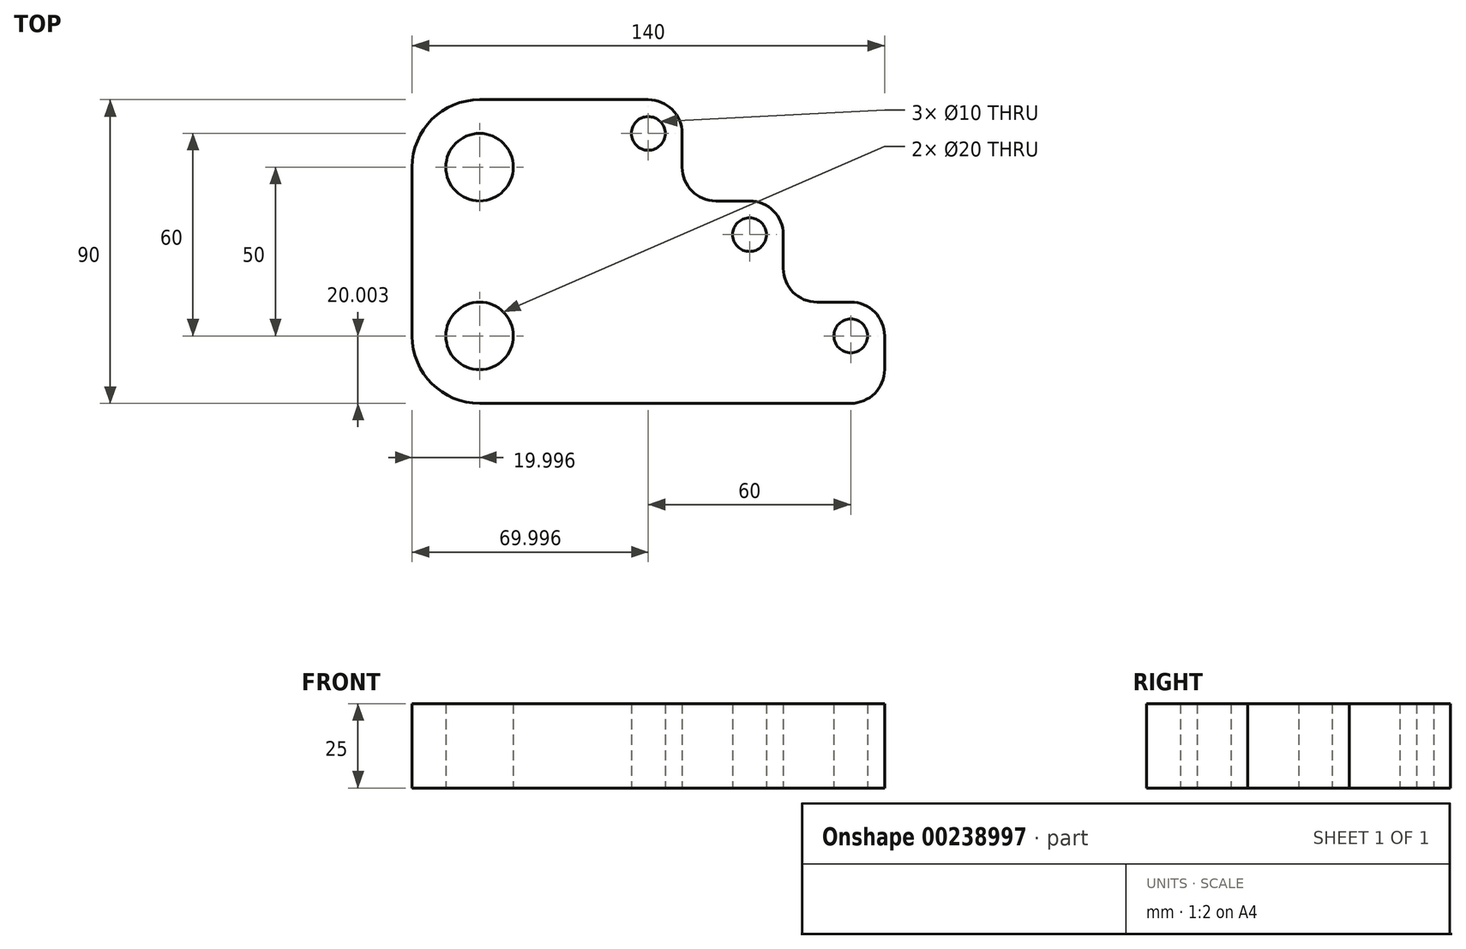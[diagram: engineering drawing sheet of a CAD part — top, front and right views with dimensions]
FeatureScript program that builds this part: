
annotation { "Feature Type Name" : "Feature", "Feature Type Description" : "" }
export const myFeature = defineFeature(function(context is Context, id is Id, definition is map)
    precondition{}
    {
        {
            var Q0;
            Q0=qCreatedBy(makeId("Top.planeOp"),FACE);
            var sketch = newSketch(context, id + "F0", { "sketchPlane" : qUnion([Q0])});
            skLineSegment(sketch, "E0", {"start": v(-71.17, 27.82) * mm, "end": v(-71.17, -22.18) * mm});
            skLineSegment(sketch, "E1", {"start": v(-51.17, -42.18) * mm, "end": v(58.83, -42.18) * mm});
            skLineSegment(sketch, "E2", {"start": v(68.83, -32.18) * mm, "end": v(68.83, -22.18) * mm});
            skLineSegment(sketch, "E3", {"start": v(58.83, -12.18) * mm, "end": v(48.83, -12.18) * mm});
            skLineSegment(sketch, "E4", {"start": v(38.83, -2.18) * mm, "end": v(38.83, 7.82) * mm});
            skLineSegment(sketch, "E5", {"start": v(28.83, 17.82) * mm, "end": v(18.83, 17.82) * mm});
            skLineSegment(sketch, "E6", {"start": v(8.83, 27.82) * mm, "end": v(8.83, 37.82) * mm});
            skLineSegment(sketch, "E7", {"start": v(-51.17, 47.82) * mm, "end": v(-1.17, 47.82) * mm});
            skPoint(sketch, "E8.visualSharp", {"position": v(8.83, 47.82) * mm});
            skArc(sketch, "E8.filletArc", {"start": v(8.83, 37.82) * mm, "mid": v(5.9, 44.9) * mm, "end": v(-1.17, 47.82) * mm});
            skPoint(sketch, "E9.visualSharp", {"position": v(8.83, 17.82) * mm});
            skArc(sketch, "E9.filletArc", {"start": v(8.83, 27.82) * mm, "mid": v(11.76, 20.75) * mm, "end": v(18.83, 17.82) * mm});
            skPoint(sketch, "E10.visualSharp", {"position": v(38.83, 17.82) * mm});
            skArc(sketch, "E10.filletArc", {"start": v(38.83, 7.82) * mm, "mid": v(35.9, 14.9) * mm, "end": v(28.83, 17.82) * mm});
            skPoint(sketch, "E11.visualSharp", {"position": v(38.83, -12.18) * mm});
            skArc(sketch, "E11.filletArc", {"start": v(38.83, -2.18) * mm, "mid": v(41.76, -9.25) * mm, "end": v(48.83, -12.18) * mm});
            skPoint(sketch, "E12.visualSharp", {"position": v(68.83, -12.18) * mm});
            skArc(sketch, "E12.filletArc", {"start": v(68.83, -22.18) * mm, "mid": v(65.9, -15.1) * mm, "end": v(58.83, -12.18) * mm});
            skPoint(sketch, "E13.visualSharp", {"position": v(68.83, -42.18) * mm});
            skArc(sketch, "E13.filletArc", {"start": v(58.83, -42.18) * mm, "mid": v(65.9, -39.25) * mm, "end": v(68.83, -32.18) * mm});
            skPoint(sketch, "E14.visualSharp", {"position": v(-71.17, 47.82) * mm});
            skArc(sketch, "E14.filletArc", {"start": v(-51.17, 47.82) * mm, "mid": v(-65.32, 41.96) * mm, "end": v(-71.17, 27.82) * mm});
            skPoint(sketch, "E15.visualSharp", {"position": v(-71.17, -42.18) * mm});
            skArc(sketch, "E15.filletArc", {"start": v(-71.17, -22.18) * mm, "mid": v(-65.32, -36.32) * mm, "end": v(-51.17, -42.18) * mm});
            skCircle(sketch, "E16", {"center": v(-51.17, 27.82) * mm, "radius": 10 * mm});
            skCircle(sketch, "E17", {"center": v(-51.17, -22.18) * mm, "radius": 10 * mm});
            skCircle(sketch, "E18", {"center": v(-1.17, 37.82) * mm, "radius": 5 * mm});
            skCircle(sketch, "E19", {"center": v(28.83, 7.82) * mm, "radius": 5 * mm});
            skCircle(sketch, "E20", {"center": v(58.83, -22.18) * mm, "radius": 5 * mm});
            skSolve(sketch);
        }
        {
            var Q0;
            Q0 = qSketchRegion(id + "F0", true);
            extrude(context, id + "F1", {"entities" : qUnion([Q0]), "depth" : 25 * mm});
        }
    });
